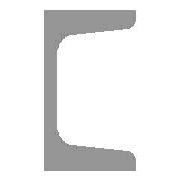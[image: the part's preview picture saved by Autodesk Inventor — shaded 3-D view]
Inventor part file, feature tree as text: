
AUTODESK INVENTOR PART (.ipt)
format: ipt  version: 2025 (Build 290162010, 162A)  size: 138,240 bytes
history: native  units: mm (DEFAULTED — no unit token found)
features: other x3, sketch x1, plane x1
ambient origin geometry x8: Origin, YZ Plane, XZ Plane, XY Plane, X Axis, Y Axis, Z Axis, Center Point
bodies: Solid1 (feature_tree), Body (feature_tree)
feature tree (5):
  other  "Driven Length"
  other  "Start plane"
  other  "End plane"
  sketch  "Sketch3"  dims[d0=5.5mm d1=40.0mm d2=45.0mm d3=7.5mm d4=19.75mm d5=2.075804mm d6=4800.0mm d7=0.0mm d23=8.0mm d24=4.0mm d25=1.43mm d26=-0.0mm d27=4800.0mm d28=90.0deg d29=4800.0mm]
  plane  "Work Plane3"
